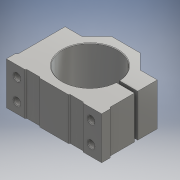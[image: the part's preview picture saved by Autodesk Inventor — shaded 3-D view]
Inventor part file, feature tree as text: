
AUTODESK INVENTOR PART (.ipt)
format: ipt  version: 2016 (Build 200138000, 138)  size: 218,624 bytes
history: native  units: mm
features: sketch x7, extrude x6, other x1, hole x1, chamfer x1
ambient origin geometry x8: Origin, YZ Plane, XZ Plane, XY Plane, X Axis, Y Axis, Z Axis, Center Point
bodies: Body1 (feature_tree), Body2 (feature_tree), Body3 (feature_tree)
feature tree (16):
  other  "Твердое тело1"
  extrude  "Выдавливание1"  Depth=90.0mm
  extrude  "Выдавливание2"  Depth=68.0mm
  extrude  "Выдавливание3"  Depth=40.0mm TaperAngle=0.0deg
  extrude  "Выдавливание4"  Depth=27.0mm
  extrude  "Выдавливание5"  Depth=55.0mm
  hole  "Отверстие1"  [1 undecoded]
  chamfer  "Фаска1"  Distance=14.0mm
  extrude  "Выдавливание6"  Depth=54.0mm
  sketch  "Эскиз1"
  sketch  "Эскиз2"
  sketch  "Эскиз3"
  sketch  "Эскиз5"
  sketch  "Эскиз6"
  sketch  "Эскиз7"
  sketch  "Эскиз8"
note: 1 required parameter value undecoded (feature->parameter linkage not recoverable at this tier; creation-order binding heuristic only, values carry confidence <= 0.55)
